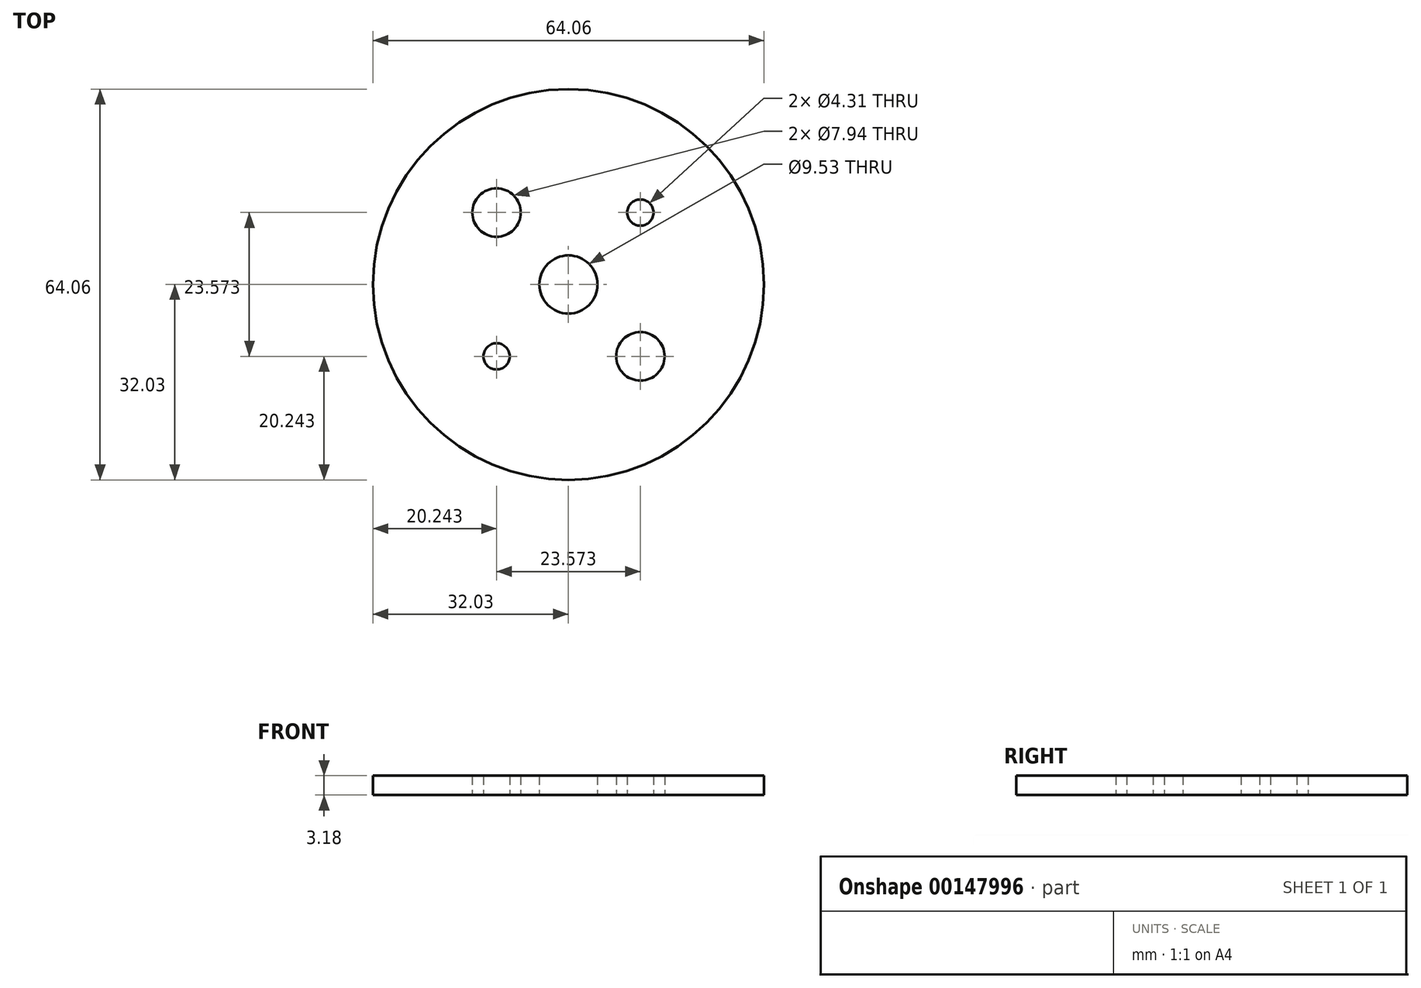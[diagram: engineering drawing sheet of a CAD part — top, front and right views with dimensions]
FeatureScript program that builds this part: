
annotation { "Feature Type Name" : "Feature", "Feature Type Description" : "" }
export const myFeature = defineFeature(function(context is Context, id is Id, definition is map)
    precondition{}
    {
        {
            var Q0;
            Q0=qCreatedBy(makeId("Top.planeOp"),FACE);
            var sketch = newSketch(context, id + "F0", { "sketchPlane" : qUnion([Q0])});
            skCircle(sketch, "E0", {"center": v(0, 0) * mm, "radius": 11.11 * mm, "construction": true});
            skLineSegment(sketch, "E1.bottom", {"start": v(11.79, -11.79) * mm, "end": v(-11.79, -11.79) * mm, "construction": true});
            skLineSegment(sketch, "E1.top", {"start": v(11.79, 11.79) * mm, "end": v(-11.79, 11.79) * mm, "construction": true});
            skLineSegment(sketch, "E1.left", {"start": v(11.79, -11.79) * mm, "end": v(11.79, 11.79) * mm, "construction": true});
            skLineSegment(sketch, "E1.right", {"start": v(-11.79, -11.79) * mm, "end": v(-11.79, 11.79) * mm, "construction": true});
            skCircle(sketch, "E2", {"center": v(-11.79, 11.79) * mm, "radius": 5.56 * mm, "construction": true});
            skCircle(sketch, "E3", {"center": v(-11.79, 11.79) * mm, "radius": 3.97 * mm});
            skCircle(sketch, "E4", {"center": v(11.79, 11.79) * mm, "radius": 2.15 * mm});
            skCircle(sketch, "E5", {"center": v(11.79, -11.79) * mm, "radius": 3.97 * mm});
            skCircle(sketch, "E6", {"center": v(-11.79, -11.79) * mm, "radius": 2.15 * mm});
            skCircle(sketch, "E7", {"center": v(0, 0) * mm, "radius": 32.03 * mm});
            skCircle(sketch, "E8", {"center": v(0, 0) * mm, "radius": 4.76 * mm});
            skSolve(sketch);
        }
        {
            var Q0;
            Q0=qSketchRegion(id+"F0",true);
            extrude(context, id + "F1", {"entities" : qUnion([Q0]), "depth" : 3.17 * mm});
        }
    });
